# Revit family: BuzziDesk_Flipflop_Revit
name_source: partatom
category: Furniture
units: mm (PartAtom-declared; Revit-internal decimal feet)

## family parameters
Always vertical = Yes
Cut with Voids When Loaded = No
OmniClass Number = 23.40.20.00
OmniClass Title = General Furniture and Specialties
Room Calculation Point = No
Shared = No
Work Plane-Based = No

## types (28) — shared parameters

## per-type parameters (varying)
| type | Height | Length Midpart | Side Type |
| Middle (50cm H x 80cm L) Sides (50cm H x 37cm L) | 50 cm | 80 cm | 50cm x 37cm Side |
| Middle (50cm H x 100cm L) Sides (50cm H x 37cm L) | 50 cm | 100 cm | 50cm x 37cm Side |
| Middle (50cm H x 120cm L) Sides (50cm H x 37cm L) | 50 cm | 120 cm | 50cm x 37cm Side |
| Middle (50cm H x 140cm L) Sides (50cm H x 37cm L) | 50 cm | 140 cm | 50cm x 37cm Side |
| Middle (50cm H x 160cm L) Sides (50cm H x 37cm L) | 50 cm | 160 cm | 50cm x 37cm Side |
| Middle (50cm H x 180cm L) Sides (50cm H x 37cm L) | 50 cm | 180 cm | 50cm x 37cm Side |
| Middle (50cm H x 200cm L) Sides (50cm H x 37cm L) | 50 cm | 200 cm | 50cm x 37cm Side |
| Middle (50cm H x 80cm L) Sides (50cm H x 50cm L) | 50 cm | 80 cm | 50cm x 50cm Side |
| Middle (50cm H x 100cm L) Sides (50cm H x 50cm L) | 50 cm | 100 cm | 50cm x 50cm Side |
| Middle (50cm H x 120cm L) Sides (50cm H x 50cm L) | 50 cm | 120 cm | 50cm x 50cm Side |
| Middle (50cm H x 140cm L) Sides (50cm H x 50cm L) | 50 cm | 140 cm | 50cm x 50cm Side |
| Middle (50cm H x 160cm L) Sides (50cm H x 50cm L) | 50 cm | 160 cm | 50cm x 50cm Side |
| Middle (50cm H x 180cm L) Sides (50cm H x 50cm L) | 50 cm | 180 cm | 50cm x 50cm Side |
| Middle (50cm H x 200cm L) Sides (50cm H x 50cm L) | 50 cm | 200 cm | 50cm x 50cm Side |
| Middle (35cm H x 80cm L) Sides (35cm H x 37cm L) | 35 cm | 80 cm | 35cm x 37cm Side |
| Middle (35cm H x 100cm L) Sides (35cm H x 37cm L) | 35 cm | 100 cm | 35cm x 37cm Side |
| Middle (35cm H x 120cm L) Sides (35cm H x 37cm L) | 35 cm | 120 cm | 35cm x 37cm Side |
| Middle (35cm H x 140cm L) Sides (35cm H x 37cm L) | 35 cm | 140 cm | 35cm x 37cm Side |
| Middle (35cm H x 160cm L) Sides (35cm H x 37cm L) | 35 cm | 160 cm | 35cm x 37cm Side |
| Middle (35cm H x 180cm L) Sides (35cm H x 37cm L) | 35 cm | 180 cm | 35cm x 37cm Side |
| Middle (35cm H x 200cm L) Sides (35cm H x 37cm L) | 35 cm | 200 cm | 35cm x 37cm Side |
| Middle (35cm H x 80cm L) Sides (35cm H x 50cm L) | 35 cm | 80 cm | 35cm x 50cm Side |
| Middle (35cm H x 100cm L) Sides (35cm H x 50cm L) | 35 cm | 100 cm | 35cm x 50cm Side |
| Middle (35cm H x 120cm L) Sides (35cm H x 50cm L) | 35 cm | 120 cm | 35cm x 50cm Side |
| Middle (35cm H x 140cm L) Sides (35cm H x 50cm L) | 35 cm | 140 cm | 35cm x 50cm Side |
| Middle (35cm H x 160cm L) Sides (35cm H x 50cm L) | 35 cm | 160 cm | 35cm x 50cm Side |
| Middle (35cm H x 180cm L) Sides (35cm H x 50cm L) | 35 cm | 180 cm | 35cm x 50cm Side |
| Middle (35cm H x 200cm L) Sides (35cm H x 50cm L) | 35 cm | 200 cm | 35cm x 50cm Side |

## geometry (parser evidence)
native form markers: Sweep x14
no freeform markers — native parametric forms only
